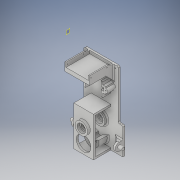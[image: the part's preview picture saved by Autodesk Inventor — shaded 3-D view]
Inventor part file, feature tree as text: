
AUTODESK INVENTOR PART (.ipt)
format: ipt  version: 2019 (Build 230136000, 136)  size: 963,072 bytes
history: native  units: in
note: dims shown in document units (in); Inventor stores cm internally (conversion verified against a paired STEP export)
features: sketch x26, extrude x25, reference x12, projected_geometry x8, other x8, mirror x3, plane x3, hole x1, fillet x1
ambient origin geometry x8: Origin, YZ Plane, XZ Plane, XY Plane, X Axis, Y Axis, Z Axis, Center Point
bodies: Solid1 (feature_tree)
feature tree (87):
  extrude  "Extrusion1"  Depth=1.5in
  extrude  "Extrusion2"  Depth=0.2in TaperAngle=0.0deg
  extrude  "Extrusion3"  Depth=0.31in
  extrude  "Extrusion4"  Depth=0.875in
  mirror  "Mirror1"
  extrude  "Extrusion5"  Depth=0.275in TaperAngle=0.0deg
  extrude  "Extrusion6"  Depth=1.6in
  extrude  "Extrusion11"  Depth=2.145in
  extrude  "Extrusion7"  Depth=0.3in
  plane  "Work Plane2"
  extrude  "Extrusion8"  Depth=0.8in TaperAngle=0.0deg
  hole  "Hole2"  [1 undecoded]
  extrude  "Extrusion13"  Depth=0.1in
  mirror  "Mirror2"
  extrude  "Extrusion14"  Depth=0.2in TaperAngle=0.0deg
  extrude  "Extrusion19"  Depth=0.41in
  sketch  "Sketch25"  dims[d72=0.691in d73=0.16in]
  plane  "Work Plane4"
  extrude  "Extrusion20"  Depth=0.16in
  extrude  "Extrusion21"  Depth=1.0in TaperAngle=0.0deg
  extrude  "Extrusion24"  Depth=3.0in
  extrude  "Extrusion23"  Depth=5.0in
  extrude  "Extrusion25"  Depth=4.475in
  extrude  "Extrusion26"  Depth=1.0in TaperAngle=0.0deg
  mirror  "Mirror3"
  extrude  "Extrusion27"  Depth=0.125in
  extrude  "Extrusion28"  Depth=0.05in
  plane  "Work Plane5"
  extrude  "Extrusion29"  Depth=0.6in
  extrude  "Extrusion30"  Depth=0.125in
  extrude  "Extrusion31"  Depth=0.5in
  extrude  "Extrusion32"  Depth=0.6in
  extrude  "Extrusion33"  Depth=0.75in TaperAngle=0.0deg
  fillet  "Fillet4"  Radius=0.125in
  sketch  "Sketch1"  dims[d2=12.0in d3=1.5in]
  sketch  "Sketch2"  dims[d4=0.2in d5=0.0in d7=0.2in d8=0.0in]
  projected_geometry  "Projected Loop1"
  sketch  "Sketch3"  dims[d9=0.2in d10=0.0in d18=0.31in]
  reference  "Reference3"
  sketch  "Sketch4"  dims[d19=0.4in d20=0.0in d25=0.875in]
  sketch  "Sketch7"  dims[d26=0.2in d27=0.275in d28=0.0in]
  sketch  "Sketch8"  dims[d29=1.575in d30=1.6in]
  sketch  "Sketch9"  dims[d31=1.25in d32=2.145in]
  projected_geometry  "Projected Loop2"
  sketch  "Sketch11"  dims[d33=0.3in d34=0.3in]
  reference  "Reference7"
  reference  "Reference8"
  sketch  "Sketch12"  dims[d35=0.2in d36=0.8in d37=0.0in]
  reference  "Reference9"
  reference  "Reference10"
  sketch  "Sketch15"  dims[d38=0.8in d39=0.0in d40=0.8in d41=0.0in]
  projected_geometry  "Projected Loop3"
  sketch  "Sketch18"  dims[d42=0.07in d43=0.224in d44=0.375in d45=0.25in d46=0.5635in d47=1.0in d48=0.8108in d56=0.1in]
  sketch  "Sketch19"  dims[d57=0.1in d58=0.2in d59=0.0in]
  projected_geometry  "Projected Loop4"
  projected_geometry  "Projected Loop5"
  sketch  "Sketch24"  dims[d66=2.628in d67=0.41in]
  projected_geometry  "Projected Loop7"
  reference  "Reference20"
  reference  "Reference21"
  reference  "Reference22"
  reference  "Reference23"
  reference  "Reference24"
  sketch  "Sketch26"  dims[d74=135.0deg d76=1.0in d77=0.0in]
  projected_geometry  "Projected Loop8"
  projected_geometry  "Projected Loop9"
  sketch  "Sketch28"  dims[d78=0.2in d79=0.0in d91=3.0in]
  sketch  "Sketch29"  dims[d92=1.0in d93=0.0in d95=5.0in]
  sketch  "Sketch30"  dims[d97=3.5in d98=4.475in]
  sketch  "Sketch31"  dims[d100=1.0in d101=0.0in d102=1.0in d103=0.0in]
  reference  "Reference25"
  reference  "Reference26"
  sketch  "Sketch32"  dims[d107=0.125in d109=0.125in]
  sketch  "Sketch33"  dims[d111=1.0in d112=0.0in d114=0.05in]
  sketch  "Sketch34"  dims[d115=1.0in d116=0.0in d117=0.6in]
  sketch  "Sketch35"  dims[d118=0.125in d119=1.0in]
  sketch  "Sketch36"  dims[d120=0.25in d121=0.0in d122=0.5in]
  sketch  "Sketch37"  dims[d123=0.25in d124=0.0in d126=0.6in]
  sketch  "Sketch39"  dims[d128=0.2in d129=1.0in d130=0.0in d131=0.125in d132=0.3in d133=0.3in d134=1.0in d135=0.0in d136=0.6in d137=2.0in d138=0.2in d139=2.0in d140=0.2in d142=3.5in d143=0.0in d144=0.2in d145=0.0in d146=0.275in d147=0.0in d148=0.2in d149=0.0in d152=0.5in d154=0.75in d155=1.5in d156=1.0in d157=0.0in]
  other  "<userpath>\OneDrive\Documents\Inventor\Mr.Green\Mr.Green.iam"
  other  "Mr.Green.iam"
  other  "Shock_Arm:1"
  other  "Front_Wheel_Drive:1"
  other  "Front_Diff:1"
  other  "Motor:1"
  other  "Assembled_Cutter:1"
  other  "Cutter:1"
note: 1 required parameter value undecoded (feature->parameter linkage not recoverable at this tier; creation-order binding heuristic only, values carry confidence <= 0.55)
